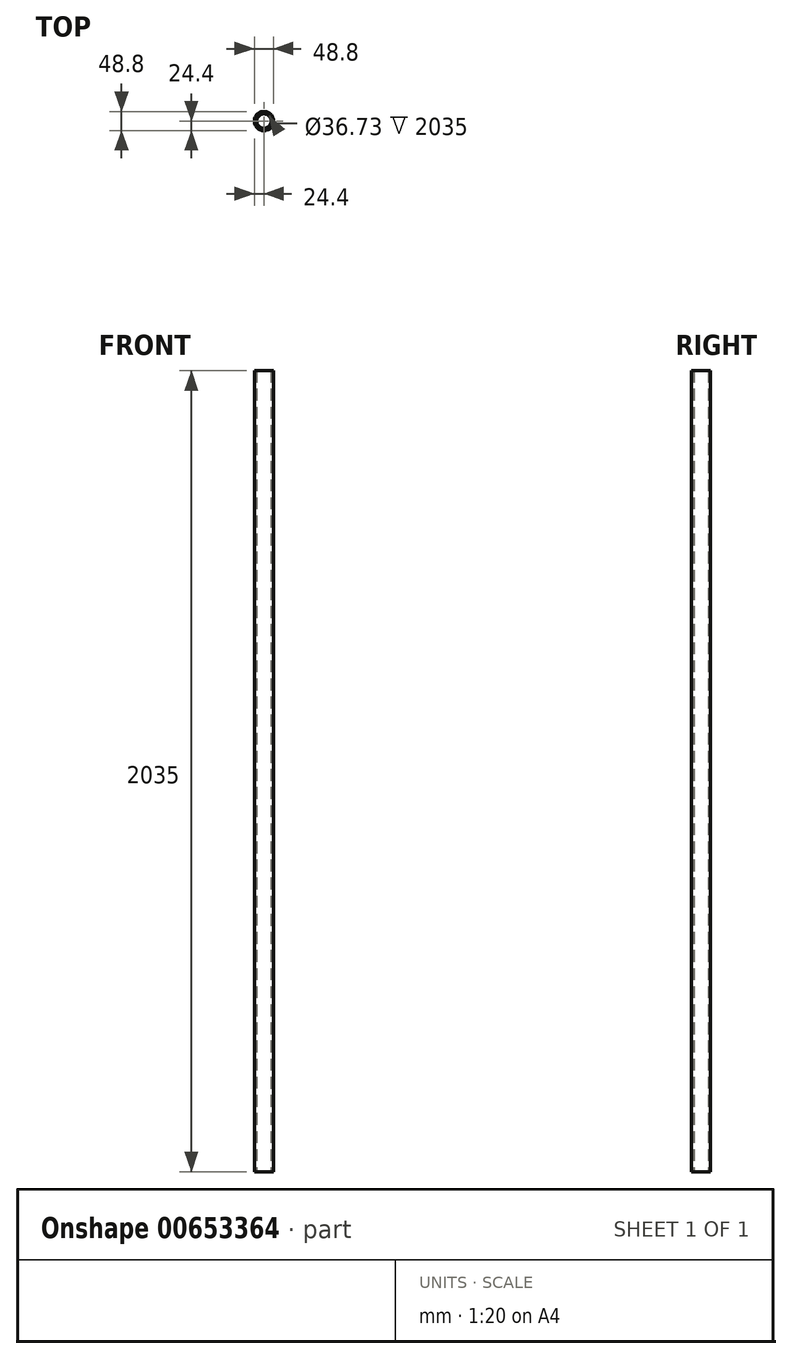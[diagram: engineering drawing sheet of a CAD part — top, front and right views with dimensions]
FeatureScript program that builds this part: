
annotation { "Feature Type Name" : "Feature", "Feature Type Description" : "" }
export const myFeature = defineFeature(function(context is Context, id is Id, definition is map)
    precondition{}
    {
        {
            var Q0;
            Q0=qCreatedBy(makeId("Top.planeOp"),FACE);
            var sketch = newSketch(context, id + "F0", { "sketchPlane" : qUnion([Q0])});
            skCircle(sketch, "E0", {"center": v(0, 0) * mm, "radius": 24.4 * mm});
            skCircle(sketch, "E1", {"center": v(0, 0) * mm, "radius": 18.37 * mm});
            skSolve(sketch);
        }
        {
            var Q0;
            Q0=qSketchRegion(id+"F0",true);
            extrude(context, id + "F1", {"entities" : qUnion([Q0]), "depth" : 60 * mm, "offsetDistance" : 25 * mm});
        }
        {
            var Q0;
            Q0=qCreatedBy(makeId("Top.planeOp"),FACE);
            var sketch = newSketch(context, id + "F2", { "sketchPlane" : qUnion([Q0])});
            skCircle(sketch, "E2.0", {"center": v(0, 0) * mm, "radius": 24.4 * mm});
            skCircle(sketch, "E3.0", {"center": v(0, 0) * mm, "radius": 18.37 * mm});
            skSolve(sketch);
        }
        {
            var Q0;
            Q0=qSketchRegion(id+"F2",true);
            extrude(context, id + "F3", {"entities" : qUnion([Q0]), "operationType" : NewBodyOperationType.ADD, "oppositeDirection" : true, "depth" : 1975 * mm, "offsetDistance" : 25 * mm});
        }
    });
